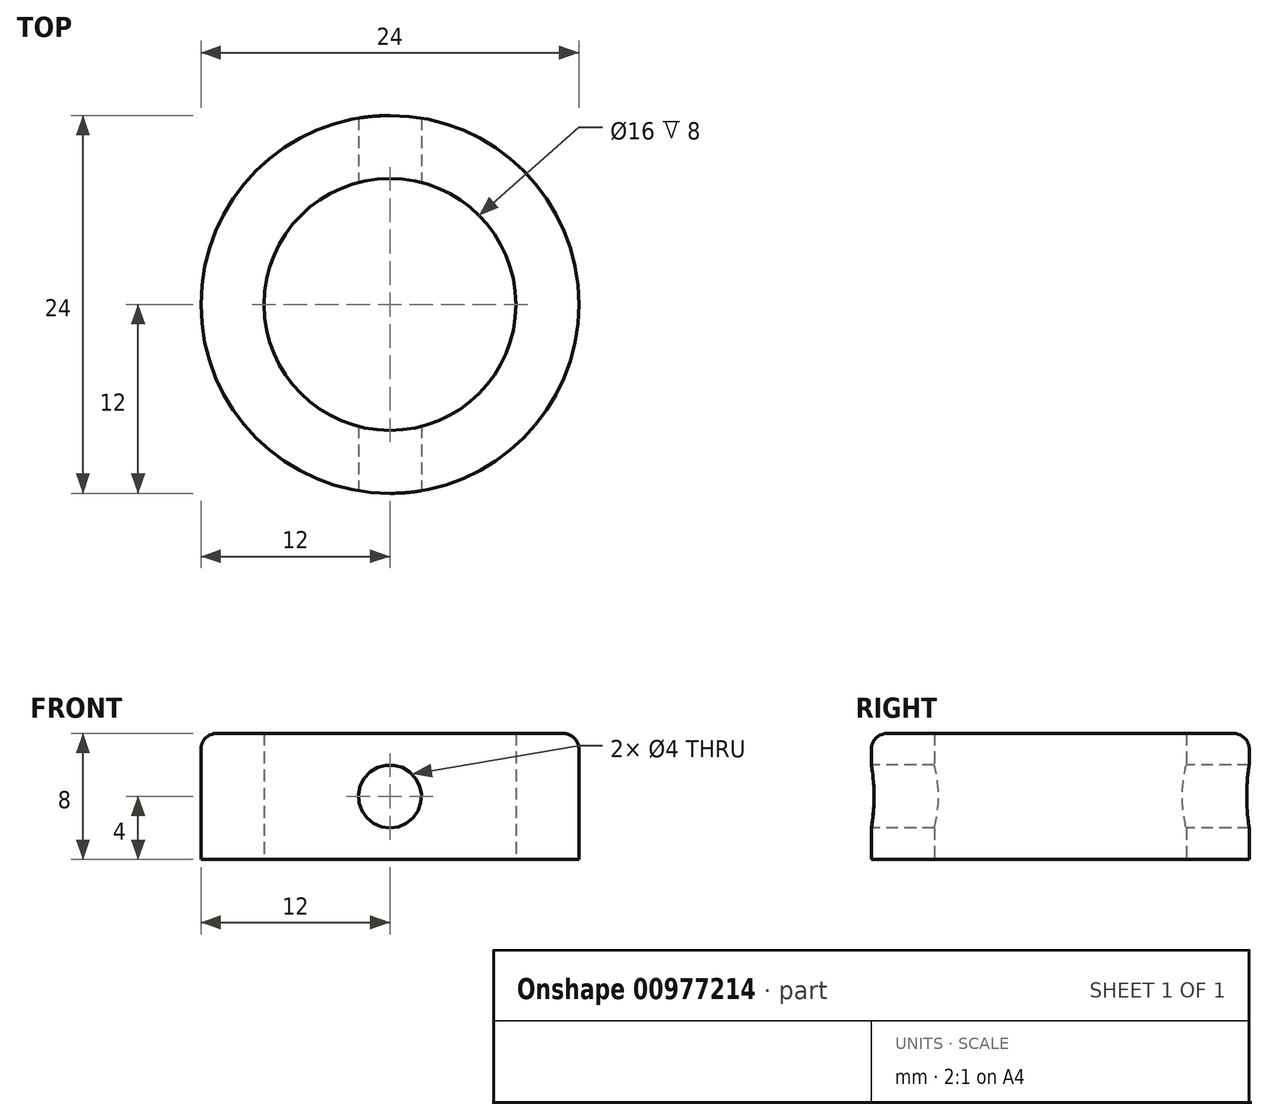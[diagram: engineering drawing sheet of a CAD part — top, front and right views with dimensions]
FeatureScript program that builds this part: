
annotation { "Feature Type Name" : "Feature", "Feature Type Description" : "" }
export const myFeature = defineFeature(function(context is Context, id is Id, definition is map)
    precondition{}
    {
        {
            var Q0;
            Q0=qCreatedBy(makeId("Top.planeOp"),FACE);
            var sketch = newSketch(context, id + "F0", { "sketchPlane" : qUnion([Q0])});
            skCircle(sketch, "E0", {"center": v(0, 0) * mm, "radius": 8 * mm});
            skCircle(sketch, "E1", {"center": v(0, 0) * mm, "radius": 12 * mm});
            skSolve(sketch);
        }
        {
            var Q0;
            Q0 = qSketchRegion(id + "F0", true);
            extrude(context, id + "F1", {"entities" : qUnion([Q0]), "endBound" : BoundingType.SYMMETRIC, "depth" : 8 * mm, "offsetDistance" : 25 * mm});
        }
        {
            var Q0;
            Q0=makeQuery(id+"F1.opExtrude","CAP_EDGE",EDGE,{"disambiguationData":[OSD([sQuery(id+"F0.wireOp",EDGE,"E1")])],"isStart":false});
            fillet(context, id + "F2", {"entities" : qUnion([Q0]), "radius" : 1 * mm, "tangentPropagation" : true, "allowEdgeOverflow" : false});
        }
        {
            var Q0;
            Q0=qCreatedBy(makeId("Front.planeOp"),FACE);
            var sketch = newSketch(context, id + "F3", { "sketchPlane" : qUnion([Q0])});
            skCircle(sketch, "E2", {"center": v(0, 0) * mm, "radius": 2 * mm});
            skSolve(sketch);
        }
        {
            var Q0;
            Q0 = qSketchRegion(id + "F3", true);
            extrude(context, id + "F4", {"entities" : qUnion([Q0]), "operationType" : NewBodyOperationType.REMOVE, "endBound" : BoundingType.SYMMETRIC, "oppositeDirection" : true, "depth" : 25 * mm, "offsetDistance" : 25 * mm});
        }
    });
